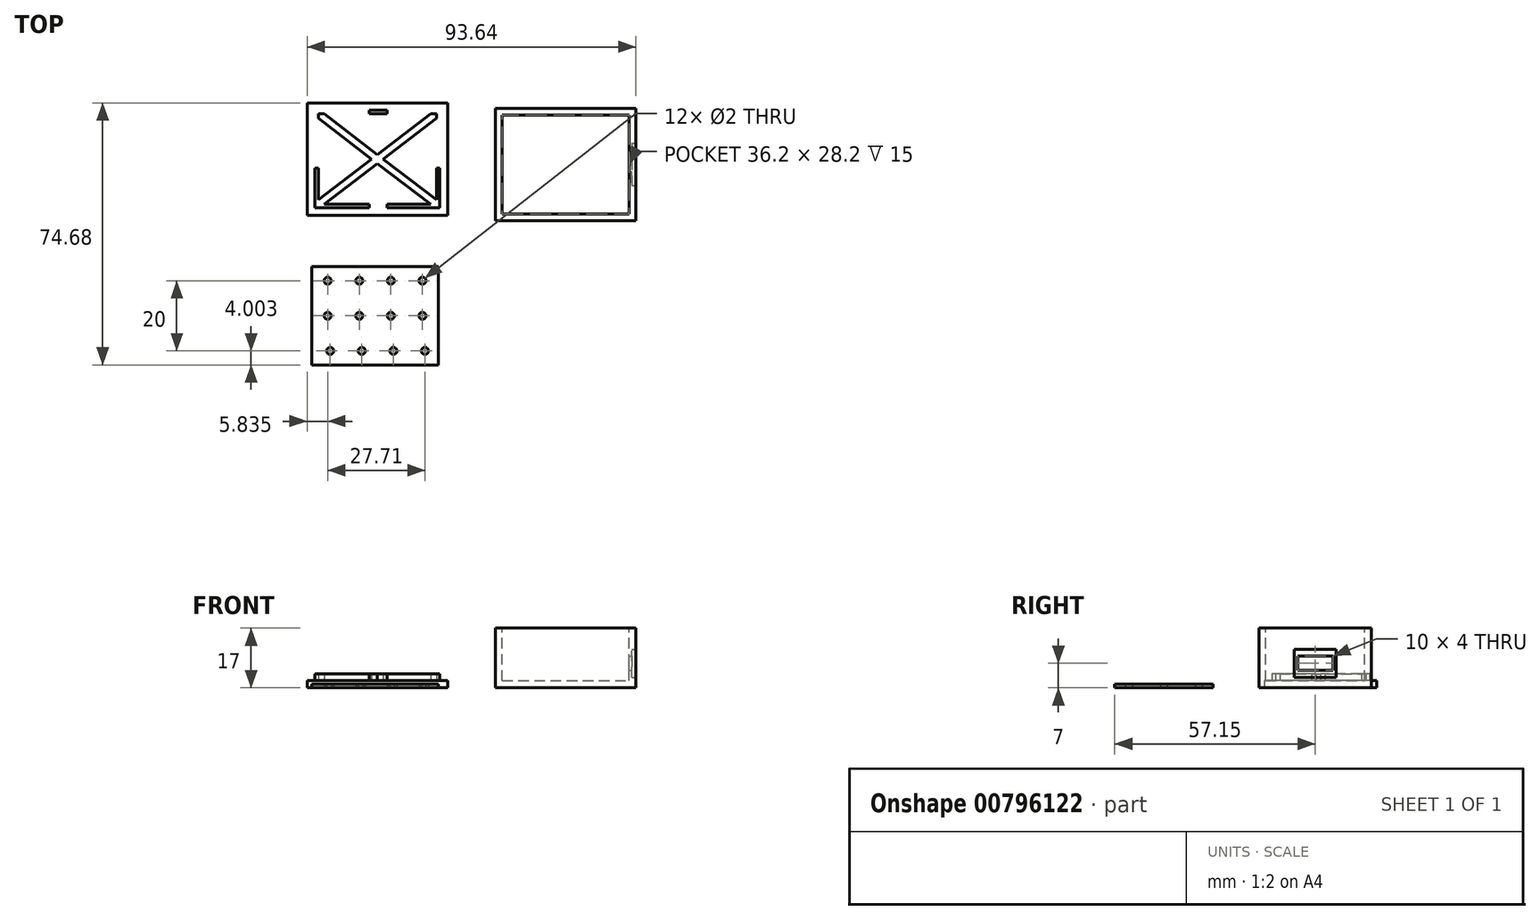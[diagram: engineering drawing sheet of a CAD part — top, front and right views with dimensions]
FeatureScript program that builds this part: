
annotation { "Feature Type Name" : "Feature", "Feature Type Description" : "" }
export const myFeature = defineFeature(function(context is Context, id is Id, definition is map)
    precondition{}
    {
        {
            var Q0;
            Q0=qCreatedBy(makeId("Top.planeOp"),FACE);
            var sketch = newSketch(context, id + "F0", { "sketchPlane" : qUnion([Q0])});
            skLineSegment(sketch, "E0.bottom", {"start": v(0, 0) * mm, "end": v(40, 0) * mm});
            skLineSegment(sketch, "E0.top", {"start": v(0, 32) * mm, "end": v(40, 32) * mm});
            skLineSegment(sketch, "E0.left", {"start": v(0, 0) * mm, "end": v(0, 32) * mm});
            skLineSegment(sketch, "E0.right", {"start": v(40, 0) * mm, "end": v(40, 32) * mm});
            skSolve(sketch);
        }
        {
            var Q0;
            Q0=qSketchRegion(id+"F0",true);
            var Q1;
            Q1=makeQuery(id+"F0.imprint","IMPRINT",FACE,{"disambiguationData":[TD([[makeQuery(id+"F0.imprint","IMPRINT",EDGE,{"derivedFrom":sQuery(id+"F0.wireOp",EDGE,"E0.bottom")}),1.0]])]});
            extrude(context, id + "F1", {"entities" : qUnion([Q0, Q1]), "depth" : 17 * mm, "offsetDistance" : 25 * mm});
        }
        {
            var Q0;
            Q0=makeQuery(id+"F1.opExtrude","CAP_FACE",FACE,{"disambiguationData":[OSD([sQuery(id+"F0.wireOp",EDGE,"E0.bottom"),sQuery(id+"F0.wireOp",EDGE,"E0.top"),sQuery(id+"F0.wireOp",EDGE,"E0.left"),sQuery(id+"F0.wireOp",EDGE,"E0.right")])],"isStart":false});
            var sketch = newSketch(context, id + "F2", { "sketchPlane" : qUnion([Q0])});
            skLineSegment(sketch, "E1.bottom", {"start": v(1.9, 1.9) * mm, "end": v(38.1, 1.9) * mm});
            skLineSegment(sketch, "E1.top", {"start": v(1.9, 30.1) * mm, "end": v(38.1, 30.1) * mm});
            skLineSegment(sketch, "E1.left", {"start": v(1.9, 1.9) * mm, "end": v(1.9, 30.1) * mm});
            skLineSegment(sketch, "E1.right", {"start": v(38.1, 1.9) * mm, "end": v(38.1, 30.1) * mm});
            skSolve(sketch);
        }
        {
            var Q0;
            Q0=makeQuery(id+"F2.imprint","IMPRINT",FACE,{"disambiguationData":[TD([[makeQuery(id+"F2.imprint","IMPRINT",EDGE,{"derivedFrom":sQuery(id+"F2.wireOp",EDGE,"E1.bottom")}),1.0]])]});
            extrude(context, id + "F3", {"entities" : qUnion([Q0]), "operationType" : NewBodyOperationType.REMOVE, "oppositeDirection" : true, "depth" : 15 * mm, "offsetDistance" : 25 * mm});
        }
        {
            var Q0;
            Q0=makeQuery(id+"F1.opExtrude","SWEPT_FACE",FACE,{"disambiguationData":[OSD([sQuery(id+"F0.wireOp",EDGE,"E0.right")])]});
            var sketch = newSketch(context, id + "F4", { "sketchPlane" : qUnion([Q0])});
            skCircle(sketch, "E2", {"center": v(16, 14) * mm, "radius": 1.5 * mm});
            skLineSegment(sketch, "E3.bottom", {"start": v(11, 9) * mm, "end": v(21, 9) * mm});
            skLineSegment(sketch, "E3.top", {"start": v(11, 5) * mm, "end": v(21, 5) * mm});
            skLineSegment(sketch, "E3.left", {"start": v(11, 9) * mm, "end": v(11, 5) * mm});
            skLineSegment(sketch, "E3.right", {"start": v(21, 9) * mm, "end": v(21, 5) * mm});
            skLineSegment(sketch, "E4.bottom", {"start": v(22, 3) * mm, "end": v(10, 3) * mm});
            skLineSegment(sketch, "E4.top", {"start": v(22, 11) * mm, "end": v(10, 11) * mm});
            skLineSegment(sketch, "E4.left", {"start": v(22, 3) * mm, "end": v(22, 11) * mm});
            skLineSegment(sketch, "E4.right", {"start": v(10, 3) * mm, "end": v(10, 11) * mm});
            skSolve(sketch);
        }
        {
            var Q0;
            Q0=makeQuery(id+"F4.imprint","IMPRINT",FACE,{"disambiguationData":[TD([[makeQuery(id+"F4.imprint","IMPRINT",EDGE,{"derivedFrom":sQuery(id+"F4.wireOp",EDGE,"E3.bottom")}),-1.0]])]});
            extrude(context, id + "F5", {"entities" : qUnion([Q0]), "operationType" : NewBodyOperationType.REMOVE, "endBound" : BoundingType.UP_TO_NEXT, "oppositeDirection" : true, "depth" : 25 * mm, "offsetDistance" : 25 * mm});
        }
        {
            var Q0;
            Q0=qCreatedBy(makeId("Top.planeOp"),FACE);
            var sketch = newSketch(context, id + "F6", { "sketchPlane" : qUnion([Q0])});
            skLineSegment(sketch, "E5.bottom", {"start": v(-13.64, 33.53) * mm, "end": v(-53.64, 33.53) * mm});
            skLineSegment(sketch, "E5.top", {"start": v(-13.64, 1.53) * mm, "end": v(-53.64, 1.53) * mm});
            skLineSegment(sketch, "E5.left", {"start": v(-13.64, 33.53) * mm, "end": v(-13.64, 1.53) * mm});
            skLineSegment(sketch, "E5.right", {"start": v(-53.64, 33.53) * mm, "end": v(-53.64, 1.53) * mm});
            skSolve(sketch);
        }
        {
            var Q0;
            Q0=makeQuery(id+"F6.imprint","IMPRINT",FACE,{"disambiguationData":[TD([[makeQuery(id+"F6.imprint","IMPRINT",EDGE,{"derivedFrom":sQuery(id+"F6.wireOp",EDGE,"E5.bottom")}),1.0]])]});
            extrude(context, id + "F7", {"entities" : qUnion([Q0]), "depth" : 2 * mm, "offsetDistance" : 25 * mm});
        }
        {
            var Q0;
            Q0=makeQuery(id+"F7.opExtrude","CAP_FACE",FACE,{"disambiguationData":[OSD([sQuery(id+"F6.wireOp",EDGE,"E5.bottom"),sQuery(id+"F6.wireOp",EDGE,"E5.top"),sQuery(id+"F6.wireOp",EDGE,"E5.left"),sQuery(id+"F6.wireOp",EDGE,"E5.right")])],"isStart":false});
            var sketch = newSketch(context, id + "F8", { "sketchPlane" : qUnion([Q0])});
            skLineSegment(sketch, "E6.bottom", {"start": v(-51.44, 31.43) * mm, "end": v(-15.84, 31.43) * mm});
            skLineSegment(sketch, "E6.top", {"start": v(-51.44, 3.63) * mm, "end": v(-15.84, 3.63) * mm});
            skLineSegment(sketch, "E6.left", {"start": v(-51.44, 31.43) * mm, "end": v(-51.44, 3.63) * mm});
            skLineSegment(sketch, "E6.right", {"start": v(-15.84, 31.43) * mm, "end": v(-15.84, 3.63) * mm});
            skLineSegment(sketch, "E7.bottom", {"start": v(-50.44, 30.43) * mm, "end": v(-16.84, 30.43) * mm});
            skLineSegment(sketch, "E7.top", {"start": v(-50.44, 4.63) * mm, "end": v(-16.84, 4.63) * mm});
            skLineSegment(sketch, "E7.left", {"start": v(-50.44, 30.43) * mm, "end": v(-50.44, 4.63) * mm});
            skLineSegment(sketch, "E7.right", {"start": v(-16.84, 30.43) * mm, "end": v(-16.84, 4.63) * mm});
            skLineSegment(sketch, "E8", {"start": v(-50.44, 30.43) * mm, "end": v(-16.84, 4.63) * mm});
            skLineSegment(sketch, "E9", {"start": v(-16.84, 30.43) * mm, "end": v(-50.44, 4.63) * mm});
            skLineSegment(sketch, "E10", {"start": v(-50.44, 29.17) * mm, "end": v(-18.48, 4.63) * mm});
            skLineSegment(sketch, "E11", {"start": v(-48.8, 30.43) * mm, "end": v(-16.84, 5.89) * mm});
            skLineSegment(sketch, "E12", {"start": v(-50.44, 5.89) * mm, "end": v(-18.48, 30.43) * mm});
            skLineSegment(sketch, "E13", {"start": v(-16.84, 29.17) * mm, "end": v(-48.8, 4.63) * mm});
            skLineSegment(sketch, "E14.bottom", {"start": v(-35.94, 31.43) * mm, "end": v(-30.94, 31.43) * mm});
            skLineSegment(sketch, "E14.top", {"start": v(-35.94, 3.63) * mm, "end": v(-30.94, 3.63) * mm});
            skLineSegment(sketch, "E14.left", {"start": v(-35.94, 31.43) * mm, "end": v(-35.94, 3.63) * mm});
            skLineSegment(sketch, "E14.right", {"start": v(-30.94, 31.43) * mm, "end": v(-30.94, 3.63) * mm});
            skLineSegment(sketch, "E15.bottom", {"start": v(-51.44, 19.93) * mm, "end": v(-15.84, 19.93) * mm});
            skLineSegment(sketch, "E15.top", {"start": v(-51.44, 14.93) * mm, "end": v(-15.84, 14.93) * mm});
            skLineSegment(sketch, "E15.left", {"start": v(-51.44, 19.93) * mm, "end": v(-51.44, 14.93) * mm});
            skLineSegment(sketch, "E15.right", {"start": v(-15.84, 19.93) * mm, "end": v(-15.84, 14.93) * mm});
            skSolve(sketch);
        }
        {
            var Q0;
            Q0=makeQuery(id+"F8.imprint","IMPRINT",FACE,{"disambiguationData":[TD([[makeQuery(id+"F8.imprint","IMPRINT",EDGE,{"derivedFrom":sQuery(id+"F8.wireOp",EDGE,"E6.bottom")}),-1.0]])]});
            var Q1;
            {var subQ1=sQuery(id+"F8.wireOp",EDGE,"E7.left");var subQ3=sQuery(id+"F8.wireOp",EDGE,"E10");var subQ4=makeQuery(id+"F8.imprint","INTERSECT",VERTEX,{"derivedFrom":[subQ1,subQ3]});Q1=makeQuery(id+"F8.imprint","IMPRINT",FACE,{"disambiguationData":[TD([[makeQuery(id+"F8.imprint","IMPRINT",EDGE,{"disambiguationData":[TD([[subQ4,-1.0]])],"derivedFrom":subQ3}),1.0]])]});}
            var Q2;
            {var subQ1=sQuery(id+"F8.wireOp",EDGE,"E7.bottom");var subQ3=sQuery(id+"F8.wireOp",EDGE,"E11");var subQ4=makeQuery(id+"F8.imprint","INTERSECT",VERTEX,{"derivedFrom":[subQ1,subQ3]});Q2=makeQuery(id+"F8.imprint","IMPRINT",FACE,{"disambiguationData":[TD([[makeQuery(id+"F8.imprint","IMPRINT",EDGE,{"disambiguationData":[TD([[subQ4,-1.0]])],"derivedFrom":subQ3}),-1.0]])]});}
            var Q3;
            {var subQ0=sQuery(id+"F8.wireOp",EDGE,"E12");var subQ1=sQuery(id+"F8.wireOp",EDGE,"E8");var subQ2=makeQuery(id+"F8.imprint","INTERSECT",VERTEX,{"derivedFrom":[subQ1,subQ0]});Q3=makeQuery(id+"F8.imprint","IMPRINT",FACE,{"disambiguationData":[TD([[makeQuery(id+"F8.imprint","IMPRINT",EDGE,{"disambiguationData":[TD([[subQ2,-1.0]])],"derivedFrom":subQ1}),1.0]])]});}
            var Q4;
            {var subQ0=sQuery(id+"F8.wireOp",EDGE,"E9");var subQ1=sQuery(id+"F8.wireOp",EDGE,"E8");var subQ2=makeQuery(id+"F8.imprint","INTERSECT",VERTEX,{"derivedFrom":[subQ1,subQ0]});Q4=makeQuery(id+"F8.imprint","IMPRINT",FACE,{"disambiguationData":[TD([[makeQuery(id+"F8.imprint","IMPRINT",EDGE,{"disambiguationData":[TD([[subQ2,-1.0]])],"derivedFrom":subQ1}),1.0]])]});}
            var Q5;
            {var subQ0=sQuery(id+"F8.wireOp",EDGE,"E12");var subQ1=sQuery(id+"F8.wireOp",EDGE,"E8");var subQ2=makeQuery(id+"F8.imprint","INTERSECT",VERTEX,{"derivedFrom":[subQ1,subQ0]});Q5=makeQuery(id+"F8.imprint","IMPRINT",FACE,{"disambiguationData":[TD([[makeQuery(id+"F8.imprint","IMPRINT",EDGE,{"disambiguationData":[TD([[subQ2,-1.0]])],"derivedFrom":subQ1}),-1.0]])]});}
            var Q6;
            {var subQ0=sQuery(id+"F8.wireOp",EDGE,"E9");var subQ1=sQuery(id+"F8.wireOp",EDGE,"E8");var subQ2=makeQuery(id+"F8.imprint","INTERSECT",VERTEX,{"derivedFrom":[subQ1,subQ0]});Q6=makeQuery(id+"F8.imprint","IMPRINT",FACE,{"disambiguationData":[TD([[makeQuery(id+"F8.imprint","IMPRINT",EDGE,{"disambiguationData":[TD([[subQ2,-1.0]])],"derivedFrom":subQ1}),-1.0]])]});}
            var Q7;
            {var subQ0=sQuery(id+"F8.wireOp",EDGE,"E9");var subQ5=sQuery(id+"F8.wireOp",EDGE,"E11");var subQ6=makeQuery(id+"F8.imprint","INTERSECT",VERTEX,{"derivedFrom":[subQ0,subQ5]});Q7=makeQuery(id+"F8.imprint","IMPRINT",FACE,{"disambiguationData":[TD([[makeQuery(id+"F8.imprint","IMPRINT",EDGE,{"disambiguationData":[TD([[subQ6,-1.0]])],"derivedFrom":subQ5}),1.0]])]});}
            var Q8;
            {var subQ0=sQuery(id+"F8.wireOp",EDGE,"E9");var subQ5=sQuery(id+"F8.wireOp",EDGE,"E11");var subQ6=makeQuery(id+"F8.imprint","INTERSECT",VERTEX,{"derivedFrom":[subQ0,subQ5]});Q8=makeQuery(id+"F8.imprint","IMPRINT",FACE,{"disambiguationData":[TD([[makeQuery(id+"F8.imprint","IMPRINT",EDGE,{"disambiguationData":[TD([[subQ6,1.0]])],"derivedFrom":subQ5}),1.0]])]});}
            var Q9;
            {var subQ0=sQuery(id+"F8.wireOp",EDGE,"E9");var subQ5=sQuery(id+"F8.wireOp",EDGE,"E10");var subQ7=makeQuery(id+"F8.imprint","INTERSECT",VERTEX,{"derivedFrom":[subQ0,subQ5]});Q9=makeQuery(id+"F8.imprint","IMPRINT",FACE,{"disambiguationData":[TD([[makeQuery(id+"F8.imprint","IMPRINT",EDGE,{"disambiguationData":[TD([[subQ7,1.0]])],"derivedFrom":subQ5}),-1.0]])]});}
            var Q10;
            {var subQ0=sQuery(id+"F8.wireOp",EDGE,"E9");var subQ5=sQuery(id+"F8.wireOp",EDGE,"E10");var subQ6=makeQuery(id+"F8.imprint","INTERSECT",VERTEX,{"derivedFrom":[subQ0,subQ5]});Q10=makeQuery(id+"F8.imprint","IMPRINT",FACE,{"disambiguationData":[TD([[makeQuery(id+"F8.imprint","IMPRINT",EDGE,{"disambiguationData":[TD([[subQ6,-1.0]])],"derivedFrom":subQ5}),-1.0]])]});}
            var Q11;
            {var subQ1=sQuery(id+"F8.wireOp",EDGE,"E7.top");var subQ3=sQuery(id+"F8.wireOp",EDGE,"E10");var subQ4=makeQuery(id+"F8.imprint","INTERSECT",VERTEX,{"derivedFrom":[subQ1,subQ3]});Q11=makeQuery(id+"F8.imprint","IMPRINT",FACE,{"disambiguationData":[TD([[makeQuery(id+"F8.imprint","IMPRINT",EDGE,{"disambiguationData":[TD([[subQ4,1.0]])],"derivedFrom":subQ3}),1.0]])]});}
            var Q12;
            {var subQ1=sQuery(id+"F8.wireOp",EDGE,"E7.right");var subQ3=sQuery(id+"F8.wireOp",EDGE,"E11");var subQ4=makeQuery(id+"F8.imprint","INTERSECT",VERTEX,{"derivedFrom":[subQ1,subQ3]});Q12=makeQuery(id+"F8.imprint","IMPRINT",FACE,{"disambiguationData":[TD([[makeQuery(id+"F8.imprint","IMPRINT",EDGE,{"disambiguationData":[TD([[subQ4,1.0]])],"derivedFrom":subQ3}),-1.0]])]});}
            var Q13;
            {var subQ0=sQuery(id+"F8.wireOp",EDGE,"E14.left");var subQ1=sQuery(id+"F8.wireOp",EDGE,"E9");var subQ2=makeQuery(id+"F8.imprint","INTERSECT",VERTEX,{"derivedFrom":[subQ1,subQ0]});Q13=makeQuery(id+"F8.imprint","IMPRINT",FACE,{"disambiguationData":[TD([[makeQuery(id+"F8.imprint","IMPRINT",EDGE,{"disambiguationData":[TD([[subQ2,-1.0]])],"derivedFrom":subQ1}),-1.0]])]});}
            var Q14;
            {var subQ0=sQuery(id+"F8.wireOp",EDGE,"E15.bottom");var subQ1=sQuery(id+"F8.wireOp",EDGE,"E8");var subQ2=makeQuery(id+"F8.imprint","INTERSECT",VERTEX,{"derivedFrom":[subQ1,subQ0]});Q14=makeQuery(id+"F8.imprint","IMPRINT",FACE,{"disambiguationData":[TD([[makeQuery(id+"F8.imprint","IMPRINT",EDGE,{"disambiguationData":[TD([[subQ2,-1.0]])],"derivedFrom":subQ1}),-1.0]])]});}
            var Q15;
            {var subQ0=sQuery(id+"F8.wireOp",EDGE,"E14.left");var subQ1=sQuery(id+"F8.wireOp",EDGE,"E8");var subQ2=makeQuery(id+"F8.imprint","INTERSECT",VERTEX,{"derivedFrom":[subQ1,subQ0]});Q15=makeQuery(id+"F8.imprint","IMPRINT",FACE,{"disambiguationData":[TD([[makeQuery(id+"F8.imprint","IMPRINT",EDGE,{"disambiguationData":[TD([[subQ2,-1.0]])],"derivedFrom":subQ1}),-1.0]])]});}
            var Q16;
            {var subQ0=sQuery(id+"F8.wireOp",EDGE,"E14.left");var subQ1=sQuery(id+"F8.wireOp",EDGE,"E8");var subQ2=makeQuery(id+"F8.imprint","INTERSECT",VERTEX,{"derivedFrom":[subQ1,subQ0]});Q16=makeQuery(id+"F8.imprint","IMPRINT",FACE,{"disambiguationData":[TD([[makeQuery(id+"F8.imprint","IMPRINT",EDGE,{"disambiguationData":[TD([[subQ2,-1.0]])],"derivedFrom":subQ1}),1.0]])]});}
            var Q17;
            {var subQ0=sQuery(id+"F8.wireOp",EDGE,"E14.left");var subQ1=sQuery(id+"F8.wireOp",EDGE,"E11");var subQ2=makeQuery(id+"F8.imprint","INTERSECT",VERTEX,{"derivedFrom":[subQ1,subQ0]});Q17=makeQuery(id+"F8.imprint","IMPRINT",FACE,{"disambiguationData":[TD([[makeQuery(id+"F8.imprint","IMPRINT",EDGE,{"disambiguationData":[TD([[subQ2,-1.0]])],"derivedFrom":subQ1}),-1.0]])]});}
            var Q18;
            {var subQ0=sQuery(id+"F8.wireOp",EDGE,"E14.left");var subQ1=sQuery(id+"F8.wireOp",EDGE,"E9");var subQ2=makeQuery(id+"F8.imprint","INTERSECT",VERTEX,{"derivedFrom":[subQ1,subQ0]});Q18=makeQuery(id+"F8.imprint","IMPRINT",FACE,{"disambiguationData":[TD([[makeQuery(id+"F8.imprint","IMPRINT",EDGE,{"disambiguationData":[TD([[subQ2,-1.0]])],"derivedFrom":subQ1}),1.0]])]});}
            var Q19;
            {var subQ1=sQuery(id+"F8.wireOp",EDGE,"E8");var subQ5=sQuery(id+"F8.wireOp",EDGE,"E13");var subQ6=makeQuery(id+"F8.imprint","INTERSECT",VERTEX,{"derivedFrom":[subQ1,subQ5]});Q19=makeQuery(id+"F8.imprint","IMPRINT",FACE,{"disambiguationData":[TD([[makeQuery(id+"F8.imprint","IMPRINT",EDGE,{"disambiguationData":[TD([[subQ6,-1.0]])],"derivedFrom":subQ1}),-1.0]])]});}
            var Q20;
            {var subQ0=sQuery(id+"F8.wireOp",EDGE,"E13");var subQ1=sQuery(id+"F8.wireOp",EDGE,"E8");var subQ2=makeQuery(id+"F8.imprint","INTERSECT",VERTEX,{"derivedFrom":[subQ1,subQ0]});Q20=makeQuery(id+"F8.imprint","IMPRINT",FACE,{"disambiguationData":[TD([[makeQuery(id+"F8.imprint","IMPRINT",EDGE,{"disambiguationData":[TD([[subQ2,-1.0]])],"derivedFrom":subQ1}),1.0]])]});}
            var Q21;
            {var subQ0=sQuery(id+"F8.wireOp",EDGE,"E14.right");var subQ1=sQuery(id+"F8.wireOp",EDGE,"E8");var subQ2=makeQuery(id+"F8.imprint","INTERSECT",VERTEX,{"derivedFrom":[subQ1,subQ0]});Q21=makeQuery(id+"F8.imprint","IMPRINT",FACE,{"disambiguationData":[TD([[makeQuery(id+"F8.imprint","IMPRINT",EDGE,{"disambiguationData":[TD([[subQ2,-1.0]])],"derivedFrom":subQ1}),1.0]])]});}
            var Q22;
            {var subQ0=sQuery(id+"F8.wireOp",EDGE,"E14.right");var subQ1=sQuery(id+"F8.wireOp",EDGE,"E8");var subQ2=makeQuery(id+"F8.imprint","INTERSECT",VERTEX,{"derivedFrom":[subQ1,subQ0]});Q22=makeQuery(id+"F8.imprint","IMPRINT",FACE,{"disambiguationData":[TD([[makeQuery(id+"F8.imprint","IMPRINT",EDGE,{"disambiguationData":[TD([[subQ2,-1.0]])],"derivedFrom":subQ1}),-1.0]])]});}
            var Q23;
            {var subQ0=sQuery(id+"F8.wireOp",EDGE,"E15.top");var subQ1=sQuery(id+"F8.wireOp",EDGE,"E10");var subQ2=makeQuery(id+"F8.imprint","INTERSECT",VERTEX,{"derivedFrom":[subQ1,subQ0]});Q23=makeQuery(id+"F8.imprint","IMPRINT",FACE,{"disambiguationData":[TD([[makeQuery(id+"F8.imprint","IMPRINT",EDGE,{"disambiguationData":[TD([[subQ2,-1.0]])],"derivedFrom":subQ1}),1.0]])]});}
            var Q24;
            {var subQ0=sQuery(id+"F8.wireOp",EDGE,"E15.bottom");var subQ1=sQuery(id+"F8.wireOp",EDGE,"E8");var subQ2=makeQuery(id+"F8.imprint","INTERSECT",VERTEX,{"derivedFrom":[subQ1,subQ0]});Q24=makeQuery(id+"F8.imprint","IMPRINT",FACE,{"disambiguationData":[TD([[makeQuery(id+"F8.imprint","IMPRINT",EDGE,{"disambiguationData":[TD([[subQ2,-1.0]])],"derivedFrom":subQ1}),1.0]])]});}
            var Q25;
            {var subQ0=sQuery(id+"F8.wireOp",EDGE,"E15.bottom");var subQ1=sQuery(id+"F8.wireOp",EDGE,"E9");var subQ2=makeQuery(id+"F8.imprint","INTERSECT",VERTEX,{"derivedFrom":[subQ1,subQ0]});Q25=makeQuery(id+"F8.imprint","IMPRINT",FACE,{"disambiguationData":[TD([[makeQuery(id+"F8.imprint","IMPRINT",EDGE,{"disambiguationData":[TD([[subQ2,-1.0]])],"derivedFrom":subQ1}),1.0]])]});}
            var Q26;
            {var subQ0=sQuery(id+"F8.wireOp",EDGE,"E15.bottom");var subQ1=sQuery(id+"F8.wireOp",EDGE,"E9");var subQ2=makeQuery(id+"F8.imprint","INTERSECT",VERTEX,{"derivedFrom":[subQ1,subQ0]});Q26=makeQuery(id+"F8.imprint","IMPRINT",FACE,{"disambiguationData":[TD([[makeQuery(id+"F8.imprint","IMPRINT",EDGE,{"disambiguationData":[TD([[subQ2,-1.0]])],"derivedFrom":subQ1}),-1.0]])]});}
            var Q27;
            {var subQ0=sQuery(id+"F8.wireOp",EDGE,"E15.bottom");var subQ1=sQuery(id+"F8.wireOp",EDGE,"E12");var subQ2=makeQuery(id+"F8.imprint","INTERSECT",VERTEX,{"derivedFrom":[subQ1,subQ0]});Q27=makeQuery(id+"F8.imprint","IMPRINT",FACE,{"disambiguationData":[TD([[makeQuery(id+"F8.imprint","IMPRINT",EDGE,{"disambiguationData":[TD([[subQ2,-1.0]])],"derivedFrom":subQ1}),-1.0]])]});}
            var Q28;
            {var subQ1=sQuery(id+"F8.wireOp",EDGE,"E12");var subQ6=sQuery(id+"F8.wireOp",EDGE,"E7.bottom");var subQ9=makeQuery(id+"F8.imprint","INTERSECT",VERTEX,{"derivedFrom":[subQ6,subQ1]});Q28=makeQuery(id+"F8.imprint","IMPRINT",FACE,{"disambiguationData":[TD([[makeQuery(id+"F8.imprint","IMPRINT",EDGE,{"disambiguationData":[TD([[subQ9,1.0]])],"derivedFrom":subQ1}),-1.0]])]});}
            var Q29;
            {var subQ1=sQuery(id+"F8.wireOp",EDGE,"E7.right");var subQ3=sQuery(id+"F8.wireOp",EDGE,"E13");var subQ4=makeQuery(id+"F8.imprint","INTERSECT",VERTEX,{"derivedFrom":[subQ1,subQ3]});Q29=makeQuery(id+"F8.imprint","IMPRINT",FACE,{"disambiguationData":[TD([[makeQuery(id+"F8.imprint","IMPRINT",EDGE,{"disambiguationData":[TD([[subQ4,-1.0]])],"derivedFrom":subQ3}),-1.0]])]});}
            var Q30;
            {var subQ1=sQuery(id+"F8.wireOp",EDGE,"E13");var subQ5=sQuery(id+"F8.wireOp",EDGE,"E7.top");var subQ6=makeQuery(id+"F8.imprint","INTERSECT",VERTEX,{"derivedFrom":[subQ5,subQ1]});Q30=makeQuery(id+"F8.imprint","IMPRINT",FACE,{"disambiguationData":[TD([[makeQuery(id+"F8.imprint","IMPRINT",EDGE,{"disambiguationData":[TD([[subQ6,1.0]])],"derivedFrom":subQ1}),-1.0]])]});}
            var Q31;
            {var subQ1=sQuery(id+"F8.wireOp",EDGE,"E7.left");var subQ3=sQuery(id+"F8.wireOp",EDGE,"E12");var subQ4=makeQuery(id+"F8.imprint","INTERSECT",VERTEX,{"derivedFrom":[subQ1,subQ3]});Q31=makeQuery(id+"F8.imprint","IMPRINT",FACE,{"disambiguationData":[TD([[makeQuery(id+"F8.imprint","IMPRINT",EDGE,{"disambiguationData":[TD([[subQ4,-1.0]])],"derivedFrom":subQ3}),-1.0]])]});}
            var Q32;
            {var subQ0=sQuery(id+"F8.wireOp",EDGE,"E7.top");var subQ1=makeQuery(id+"F8.imprint","INTERSECT",VERTEX,{"derivedFrom":[subQ0,sQuery(id+"F8.wireOp",EDGE,"E13")]});Q32=makeQuery(id+"F8.imprint","IMPRINT",FACE,{"disambiguationData":[TD([[makeQuery(id+"F8.imprint","IMPRINT",EDGE,{"disambiguationData":[TD([[subQ1,-1.0]])],"derivedFrom":subQ0}),-1.0]])]});}
            var Q33;
            {var subQ0=sQuery(id+"F8.wireOp",EDGE,"E7.top");var subQ1=makeQuery(id+"F8.imprint","INTERSECT",VERTEX,{"derivedFrom":[subQ0,sQuery(id+"F8.wireOp",EDGE,"E10")]});Q33=makeQuery(id+"F8.imprint","IMPRINT",FACE,{"disambiguationData":[TD([[makeQuery(id+"F8.imprint","IMPRINT",EDGE,{"disambiguationData":[TD([[subQ1,1.0]])],"derivedFrom":subQ0}),-1.0]])]});}
            var Q34;
            {var subQ0=sQuery(id+"F8.wireOp",EDGE,"E15.top");var subQ1=sQuery(id+"F8.wireOp",EDGE,"E13");var subQ2=makeQuery(id+"F8.imprint","INTERSECT",VERTEX,{"derivedFrom":[subQ1,subQ0]});Q34=makeQuery(id+"F8.imprint","IMPRINT",FACE,{"disambiguationData":[TD([[makeQuery(id+"F8.imprint","IMPRINT",EDGE,{"disambiguationData":[TD([[subQ2,-1.0]])],"derivedFrom":subQ1}),-1.0]])]});}
            extrude(context, id + "F9", {"entities" : qUnion([Q0, Q1, Q2, Q3, Q4, Q5, Q6, Q7, Q8, Q9, Q10, Q11, Q12, Q13, Q14, Q15, Q16, Q17, Q18, Q19, Q20, Q21, Q22, Q23, Q24, Q25, Q26, Q27, Q28, Q29, Q30, Q31, Q32, Q33, Q34]), "operationType" : NewBodyOperationType.ADD, "depth" : 2 * mm, "offsetDistance" : 25 * mm});
        }
        {
            var Q0;
            Q0=makeQuery(id+"F4.imprint","IMPRINT",FACE,{"disambiguationData":[TD([[makeQuery(id+"F4.imprint","IMPRINT",EDGE,{"derivedFrom":sQuery(id+"F4.wireOp",EDGE,"E3.bottom")}),1.0]])]});
            extrude(context, id + "F10", {"entities" : qUnion([Q0]), "operationType" : NewBodyOperationType.REMOVE, "oppositeDirection" : true, "depth" : 1.2 * mm, "offsetDistance" : 25 * mm});
        }
        {
            var Q0;
            Q0=qCreatedBy(makeId("Top.planeOp"),FACE);
            var sketch = newSketch(context, id + "F11", { "sketchPlane" : qUnion([Q0])});
            skLineSegment(sketch, "E16.bottom", {"start": v(-52.3, -41.15) * mm, "end": v(-16.3, -41.15) * mm});
            skLineSegment(sketch, "E16.top", {"start": v(-52.3, -13.15) * mm, "end": v(-16.3, -13.15) * mm});
            skLineSegment(sketch, "E16.left", {"start": v(-52.3, -41.15) * mm, "end": v(-52.3, -13.15) * mm});
            skLineSegment(sketch, "E16.right", {"start": v(-16.3, -41.15) * mm, "end": v(-16.3, -13.15) * mm});
            skCircle(sketch, "E17", {"center": v(-47.8, -17.15) * mm, "radius": 1 * mm});
            skCircle(sketch, "E18.1.0.0", {"center": v(-38.8, -17.15) * mm, "radius": 1 * mm});
            skCircle(sketch, "E18.2.0.0", {"center": v(-29.8, -17.15) * mm, "radius": 1 * mm});
            skCircle(sketch, "E18.3.0.0", {"center": v(-20.8, -17.15) * mm, "radius": 1 * mm});
            skLineSegment(sketch, "E18.direction1", {"start": v(-47.8, -17.15) * mm, "end": v(-38.8, -17.15) * mm, "construction": true});
            skCircle(sketch, "E19", {"center": v(-47.8, -27.15) * mm, "radius": 1 * mm});
            skCircle(sketch, "E20.1.0.0", {"center": v(-38.8, -27.15) * mm, "radius": 1 * mm});
            skCircle(sketch, "E20.2.0.0", {"center": v(-29.8, -27.15) * mm, "radius": 1 * mm});
            skCircle(sketch, "E20.3.0.0", {"center": v(-20.8, -27.15) * mm, "radius": 1 * mm});
            skLineSegment(sketch, "E20.direction1", {"start": v(-47.8, -27.15) * mm, "end": v(-38.8, -27.15) * mm, "construction": true});
            skCircle(sketch, "E21", {"center": v(-47.1, -37.15) * mm, "radius": 1 * mm});
            skCircle(sketch, "E22.1.0.0", {"center": v(-38.1, -37.15) * mm, "radius": 1 * mm});
            skCircle(sketch, "E22.2.0.0", {"center": v(-29.1, -37.15) * mm, "radius": 1 * mm});
            skCircle(sketch, "E22.3.0.0", {"center": v(-20.1, -37.15) * mm, "radius": 1 * mm});
            skLineSegment(sketch, "E22.direction1", {"start": v(-47.1, -37.15) * mm, "end": v(-38.1, -37.15) * mm, "construction": true});
            skSolve(sketch);
        }
        {
            var Q0;
            Q0=makeQuery(id+"F11.imprint","IMPRINT",FACE,{"disambiguationData":[TD([[makeQuery(id+"F11.imprint","IMPRINT",EDGE,{"derivedFrom":sQuery(id+"F11.wireOp",EDGE,"E16.bottom")}),1.0]])]});
            extrude(context, id + "F12", {"entities" : qUnion([Q0]), "depth" : 1 * mm, "offsetDistance" : 25 * mm});
        }
    });
